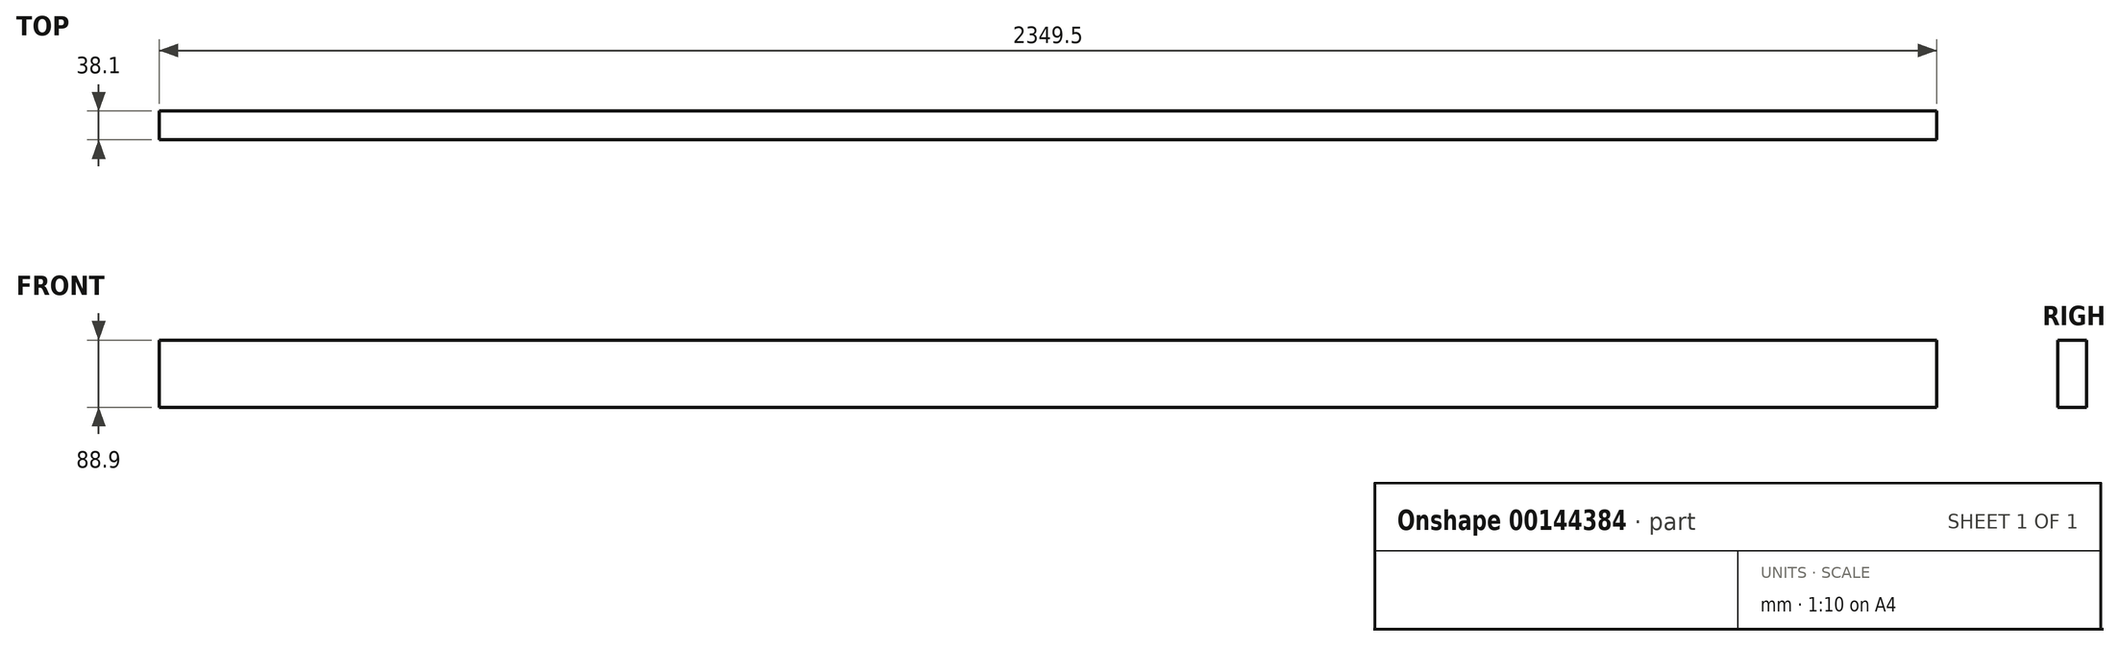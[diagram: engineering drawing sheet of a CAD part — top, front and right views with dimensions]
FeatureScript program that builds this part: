
annotation { "Feature Type Name" : "Feature", "Feature Type Description" : "" }
export const myFeature = defineFeature(function(context is Context, id is Id, definition is map)
    precondition{}
    {
        {
            var Q0;
            Q0=qCreatedBy(makeId("Top.planeOp"),FACE);
            var sketch = newSketch(context, id + "F0", { "sketchPlane" : qUnion([Q0])});
            skLineSegment(sketch, "E0.bottom", {"start": v(-1174.75, -19.05) * mm, "end": v(1174.75, -19.05) * mm});
            skLineSegment(sketch, "E0.top", {"start": v(-1174.75, 19.05) * mm, "end": v(1174.75, 19.05) * mm});
            skLineSegment(sketch, "E0.left", {"start": v(-1174.75, -19.05) * mm, "end": v(-1174.75, 19.05) * mm});
            skLineSegment(sketch, "E0.right", {"start": v(1174.75, -19.05) * mm, "end": v(1174.75, 19.05) * mm});
            skPoint(sketch, "E0.middle", {"position": v(0, 0) * mm});
            skSolve(sketch);
        }
        {
            var Q0;
            Q0 = qSketchRegion(id + "F0", true);
            extrude(context, id + "F1", {"entities" : qUnion([Q0]), "depth" : 88.9 * mm});
        }
    });
